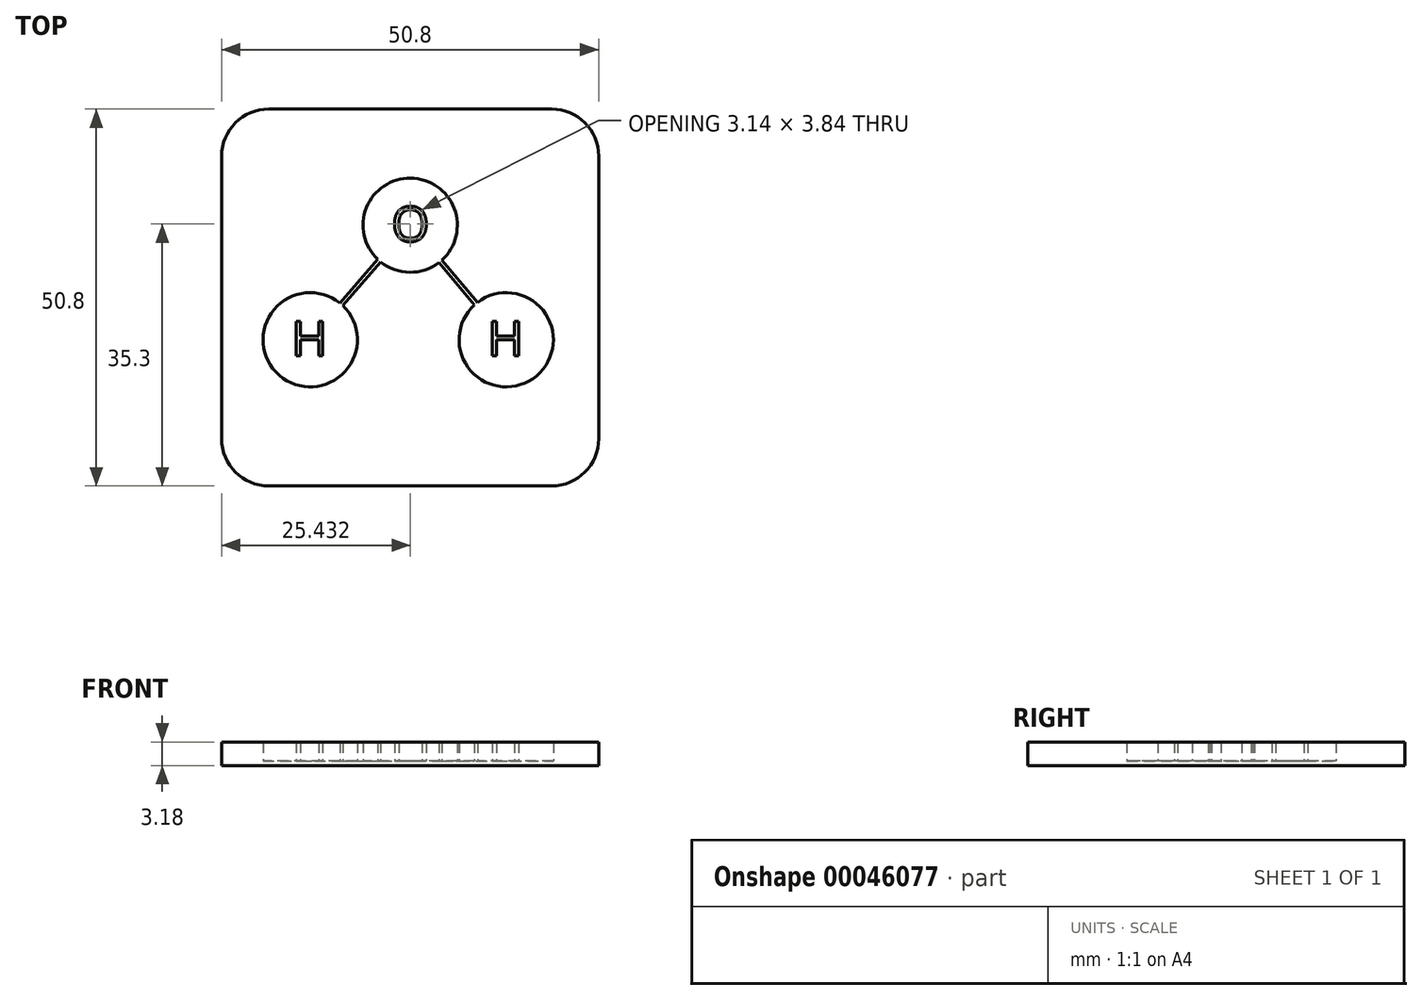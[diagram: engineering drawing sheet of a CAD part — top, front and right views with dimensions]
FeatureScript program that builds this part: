
annotation { "Feature Type Name" : "Feature", "Feature Type Description" : "" }
export const myFeature = defineFeature(function(context is Context, id is Id, definition is map)
    precondition{}
    {
        {
            var Q0;
            Q0=qCreatedBy(makeId("Top.planeOp"),FACE);
            var sketch = newSketch(context, id + "F0", { "sketchPlane" : qUnion([Q0])});
            skLineSegment(sketch, "E0.rect.bottom", {"start": v(-19.05, 25.4) * mm, "end": v(19.05, 25.4) * mm});
            skLineSegment(sketch, "E0.rect.top", {"start": v(-19.05, -25.4) * mm, "end": v(19.05, -25.4) * mm});
            skLineSegment(sketch, "E0.rect.left", {"start": v(-25.4, 19.05) * mm, "end": v(-25.4, -19.05) * mm});
            skLineSegment(sketch, "E0.rect.right", {"start": v(25.4, 19.05) * mm, "end": v(25.4, -19.05) * mm});
            skPoint(sketch, "E0.rect.middle", {"position": v(0, 0) * mm});
            skPoint(sketch, "E1.visualSharp", {"position": v(-25.4, 25.4) * mm});
            skArc(sketch, "E1.filletArc", {"start": v(-19.05, 25.4) * mm, "mid": v(-23.54, 23.54) * mm, "end": v(-25.4, 19.05) * mm});
            skPoint(sketch, "E2.visualSharp", {"position": v(25.4, 25.4) * mm});
            skArc(sketch, "E2.filletArc", {"start": v(25.4, 19.05) * mm, "mid": v(23.54, 23.54) * mm, "end": v(19.05, 25.4) * mm});
            skPoint(sketch, "E3.visualSharp", {"position": v(25.4, -25.4) * mm});
            skArc(sketch, "E3.filletArc", {"start": v(19.05, -25.4) * mm, "mid": v(23.54, -23.54) * mm, "end": v(25.4, -19.05) * mm});
            skPoint(sketch, "E4.visualSharp", {"position": v(-25.4, -25.4) * mm});
            skArc(sketch, "E4.filletArc", {"start": v(-25.4, -19.05) * mm, "mid": v(-23.54, -23.54) * mm, "end": v(-19.05, -25.4) * mm});
            skSolve(sketch);
        }
        {
            var Q0;
            Q0 = qSketchRegion(id + "F0", true);
            extrude(context, id + "F1", {"entities" : qUnion([Q0]), "depth" : 0.64 * mm});
        }
        {
            var Q0;
            Q0=makeQuery(id+"F1.opExtrude","CAP_FACE",FACE,{"disambiguationData":[OSD([sQuery(id+"F0.wireOp",EDGE,"E0.rect.bottom"),sQuery(id+"F0.wireOp",EDGE,"E0.rect.top"),sQuery(id+"F0.wireOp",EDGE,"E0.rect.left"),sQuery(id+"F0.wireOp",EDGE,"E0.rect.right"),sQuery(id+"F0.wireOp",EDGE,"E1.filletArc"),sQuery(id+"F0.wireOp",EDGE,"E2.filletArc"),sQuery(id+"F0.wireOp",EDGE,"E3.filletArc"),sQuery(id+"F0.wireOp",EDGE,"E4.filletArc")])],"isStart":false});
            var sketch = newSketch(context, id + "F2", { "sketchPlane" : qUnion([Q0])});
            skArc(sketch, "E5", {"start": v(-3.98, 4.8) * mm, "mid": v(-0.06, 3.4) * mm, "end": v(3.88, 4.72) * mm});
            skArc(sketch, "E6", {"start": v(-9.48, -0.75) * mm, "mid": v(-17.63, -10.48) * mm, "end": v(-9.1, -1.08) * mm});
            skArc(sketch, "E7", {"start": v(8.67, -1) * mm, "mid": v(17.02, -10.56) * mm, "end": v(9.06, -0.67) * mm});
            skPoint(sketch, "E8.end.orphan", {"position": v(-5.1, 5.97) * mm});
            skPoint(sketch, "E8.start.orphan", {"position": v(-10.65, 0) * mm});
            skPoint(sketch, "E9.start.orphan", {"position": v(-1.84, 3.67) * mm});
            skPoint(sketch, "E10.start.orphan", {"position": v(1.84, 3.67) * mm});
            skPoint(sketch, "E11.end.orphan", {"position": v(10.13, 0) * mm});
            skPoint(sketch, "E11.start.orphan", {"position": v(5.1, 5.97) * mm});
            skLineSegment(sketch, "E12.0", {"start": v(-9.1, -1.08) * mm, "end": v(-3.98, 4.8) * mm});
            skLineSegment(sketch, "E13.0", {"start": v(-9.48, -0.74) * mm, "end": v(-4.36, 5.13) * mm});
            skLineSegment(sketch, "E14.0", {"start": v(4.27, 5.05) * mm, "end": v(9.06, -0.67) * mm});
            skLineSegment(sketch, "E15.0", {"start": v(3.88, 4.72) * mm, "end": v(8.67, -1) * mm});
            skLineSegment(sketch, "E16", {"start": v(-3.98, 4.8) * mm, "end": v(-3.98, 4.8) * mm});
            skLineSegment(sketch, "E17", {"start": v(-4.36, 5.13) * mm, "end": v(-4.36, 5.13) * mm});
            skLineSegment(sketch, "E18", {"start": v(-9.48, -0.74) * mm, "end": v(-9.48, -0.75) * mm});
            skLineSegment(sketch, "E19", {"start": v(-9.1, -1.08) * mm, "end": v(-9.1, -1.08) * mm});
            skArc(sketch, "E20.trimOffspring", {"start": v(4.27, 5.05) * mm, "mid": v(0.06, 16.1) * mm, "end": v(-4.36, 5.13) * mm});
            skSolve(sketch);
        }
        {
            var Q0;
            Q0 = qSketchRegion(id + "F2", true);
            var Q1;
            Q1 = qSketchRegion(id + "F4", true);
            var Q2;
            Q2=makeQuery(id+"F1.opExtrude","CAP_FACE",FACE,{"disambiguationData":[OSD([sQuery(id+"F0.wireOp",EDGE,"E0.rect.bottom"),sQuery(id+"F0.wireOp",EDGE,"E0.rect.top"),sQuery(id+"F0.wireOp",EDGE,"E0.rect.left"),sQuery(id+"F0.wireOp",EDGE,"E0.rect.right"),sQuery(id+"F0.wireOp",EDGE,"E1.filletArc"),sQuery(id+"F0.wireOp",EDGE,"E2.filletArc"),sQuery(id+"F0.wireOp",EDGE,"E3.filletArc"),sQuery(id+"F0.wireOp",EDGE,"E4.filletArc")])],"isStart":false});
            extrude(context, id + "F3", {"entities" : qUnion([Q0, Q1]), "operationType" : NewBodyOperationType.REMOVE, "depth" : 3.17 * mm});
        }
        {
            var Q0;
            Q0=makeQuery(id+"F1.opExtrude","CAP_FACE",FACE,{"disambiguationData":[OSD([sQuery(id+"F0.wireOp",EDGE,"E0.rect.bottom"),sQuery(id+"F0.wireOp",EDGE,"E0.rect.top"),sQuery(id+"F0.wireOp",EDGE,"E0.rect.left"),sQuery(id+"F0.wireOp",EDGE,"E0.rect.right"),sQuery(id+"F0.wireOp",EDGE,"E1.filletArc"),sQuery(id+"F0.wireOp",EDGE,"E2.filletArc"),sQuery(id+"F0.wireOp",EDGE,"E3.filletArc"),sQuery(id+"F0.wireOp",EDGE,"E4.filletArc")])],"isStart":false});
            var sketch = newSketch(context, id + "F4", { "sketchPlane" : qUnion([Q0])});
            skText(sketch, "E21", { "text": "H", "fontName": "OpenSans-Regular.ttf"});
            skText(sketch, "E22", { "text": "H", "fontName": "OpenSans-Regular.ttf"});
            skText(sketch, "E23", { "text": "O", "fontName": "OpenSans-Regular.ttf"});
            const initialGuessF4  = {"E21": [-0.01597, -0.00788, 1, 0, 0.0047], "E22": [0.01043, -0.00788, 1, 0, 0.0047], "E23": [-0.00251, 0.00757, 1, 0, 0.0047]};
            skSetInitialGuess(sketch, initialGuessF4);
            skSolve(sketch);
        }
        {
            var Q0;
            Q0 = qSketchRegion(id + "F4", true);
            extrude(context, id + "F5", {"entities" : qUnion([Q0]), "depth" : 2.54 * mm});
        }
        {
            var Q0;
            Q0=makeQuery(id+"F2.imprint","IMPRINT",FACE,{"disambiguationData":[TD([[makeQuery(id+"F2.imprint","IMPRINT",EDGE,{"derivedFrom":sQuery(id+"F2.wireOp",EDGE,"E5")}),-1.0]])]});
            extrude(context, id + "F6", {"entities" : qUnion([Q0]), "operationType" : NewBodyOperationType.ADD, "depth" : 2.54 * mm});
        }
    });
